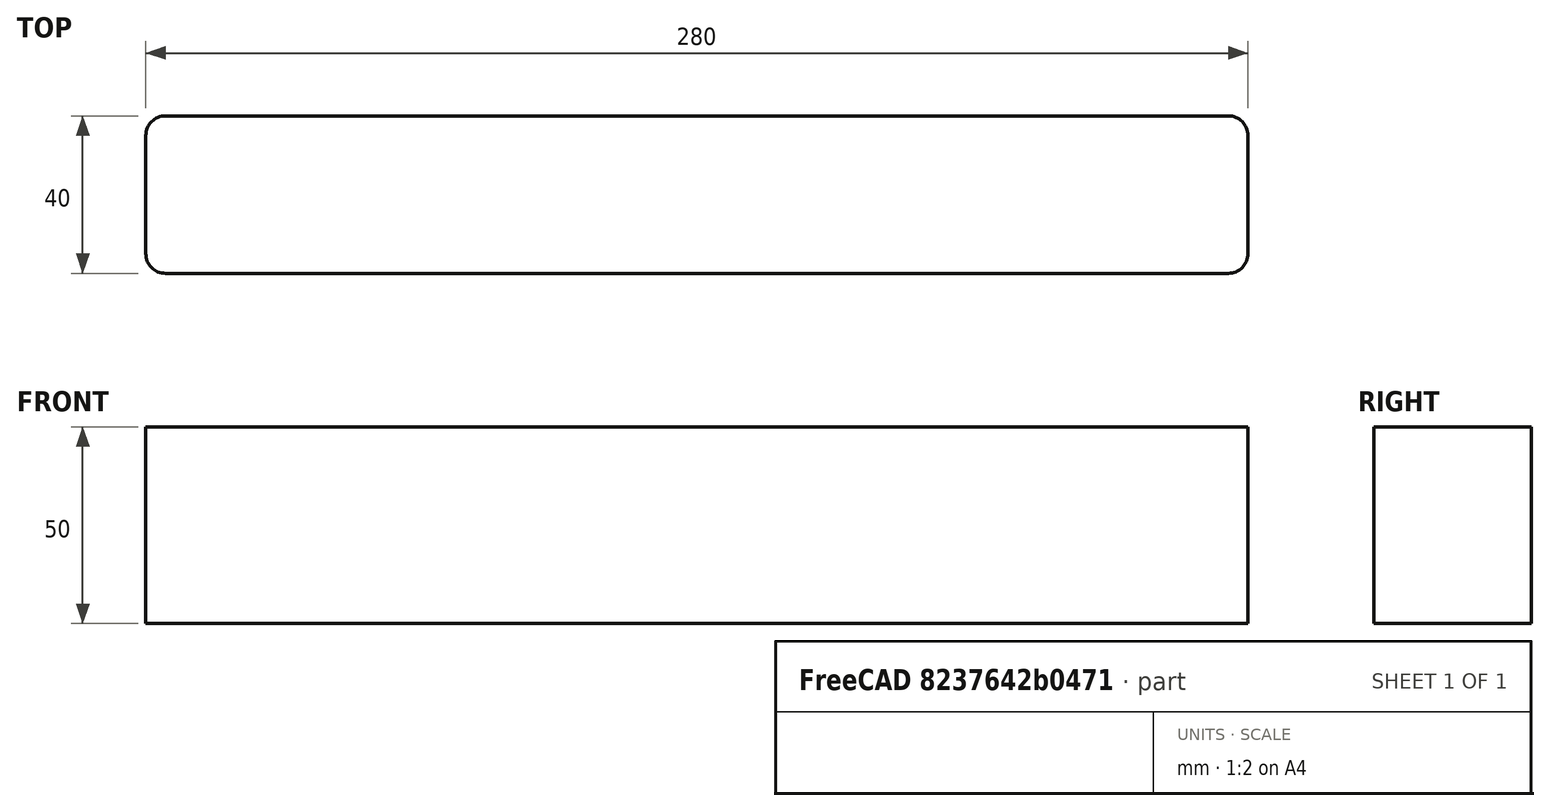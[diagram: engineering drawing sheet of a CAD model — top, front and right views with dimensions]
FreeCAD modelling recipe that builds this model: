
FCSTD DOCUMENT  (FreeCAD 0.18R4 (GitTag))
Label: v1
License: All rights reserved
LicenseURL: http://en.wikipedia.org/wiki/All_rights_reserved
objects: Sketcher::SketchObject×1, PartDesign::Pad×1, PartDesign::Body×1
note: 4 computed .brp shape members not serialized (recipe doc carries the construction recipe); baked Part::Feature solids carry a one-line shape summary decoded from their .brp

FEATURE [Sketcher::SketchObject] Sketch
  MapMode = 5
  Support = -> [XY_Plane]
  sketch-geometry (8):
    g0: LineSegment StartX=-9e-16 StartY=0 StartZ=0 EndX=270 EndY=0 EndZ=0
    g1: LineSegment StartX=275 StartY=5 StartZ=0 EndX=275 EndY=35 EndZ=0
    g2: LineSegment StartX=270 StartY=40 StartZ=0 EndX=0 EndY=40 EndZ=0
    g3: LineSegment StartX=-5 StartY=35 StartZ=0 EndX=-5 EndY=5 EndZ=0
    g4: ArcOfCircle CenterX=5e-16 CenterY=35 CenterZ=0 NormalX=0 NormalY=0 NormalZ=1 AngleXU=0 Radius=5 StartAngle=1.5708 EndAngle=3.14159
    g5: ArcOfCircle CenterX=0 CenterY=5 CenterZ=0 NormalX=0 NormalY=0 NormalZ=1 AngleXU=0 Radius=5 StartAngle=3.14159 EndAngle=4.71239
    g6: ArcOfCircle CenterX=270 CenterY=5 CenterZ=0 NormalX=0 NormalY=0 NormalZ=1 AngleXU=0 Radius=5 StartAngle=4.71239 EndAngle=6.28319
    g7: ArcOfCircle CenterX=270 CenterY=35 CenterZ=0 NormalX=0 NormalY=0 NormalZ=1 AngleXU=0 Radius=5 StartAngle=7e-16 EndAngle=1.5708
  constraints (19):
    c: Horizontal(g0)
    c: Horizontal(g2)
    c: Vertical(g1)
    c: Vertical(g3)
    c: Tangent(g3,g4) = -1.5708
    c: Tangent(g2,g4) = -1.5708
    c: DistanceX(g3,g4) = 5
    c: Tangent(g3,g5) = -1.5708
    c: Tangent(g0,g5) = -1.5708
    c: Tangent(g0,g6) = -1.5708
    c: Tangent(g1,g6) = -1.5708
    c: Tangent(g2,g7) = -1.5708
    c: Tangent(g1,g7) = -1.5708
    c: DistanceX(g3,g5) = 5
    c: DistanceX(g6,g1) = 5
    c: DistanceX(g7,g1) = 5
    c: DistanceY(g0,g2) = 40
    c: DistanceX(g3,g1) = 280
    c: Coincident(g0,g-1)
FEATURE [PartDesign::Pad] Pad001
  Length = 50
  Length2 = 100
  Profile = -> Sketch
  Type = 0
FEATURE [PartDesign::Body] Body
  Group = -> [Sketch,Pad001]
  Origin = -> Origin
  Tip = -> Pad001
